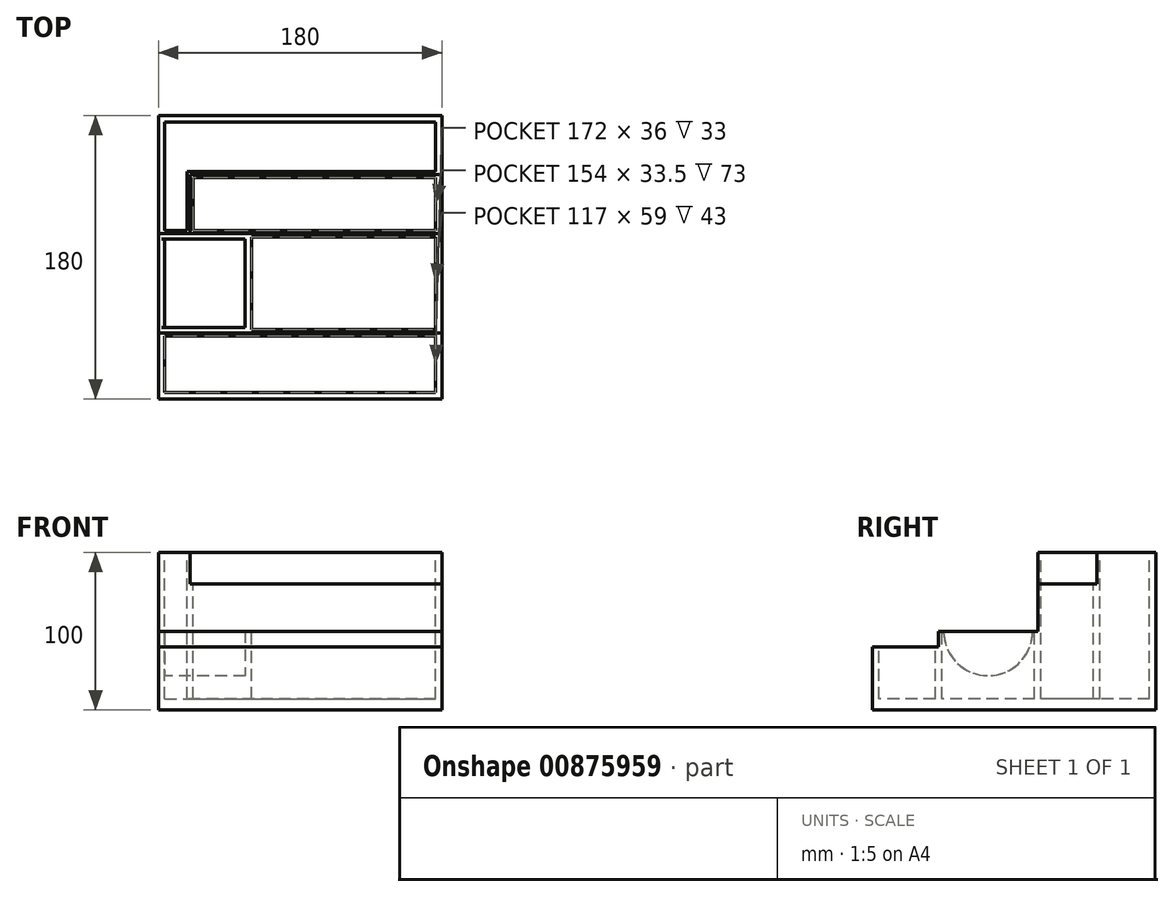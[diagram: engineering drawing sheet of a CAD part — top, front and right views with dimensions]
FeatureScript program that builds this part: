
annotation { "Feature Type Name" : "Feature", "Feature Type Description" : "" }
export const myFeature = defineFeature(function(context is Context, id is Id, definition is map)
    precondition{}
    {
        {
            var Q0;
            Q0=qCreatedBy(makeId("Top.planeOp"),FACE);
            var sketch = newSketch(context, id + "F0", { "sketchPlane" : qUnion([Q0])});
            skLineSegment(sketch, "E0.bottom", {"start": v(90, 90) * mm, "end": v(-90, 90) * mm});
            skLineSegment(sketch, "E0.top", {"start": v(90, -90) * mm, "end": v(-90, -90) * mm});
            skLineSegment(sketch, "E0.left", {"start": v(90, 90) * mm, "end": v(90, -90) * mm});
            skLineSegment(sketch, "E0.right", {"start": v(-90, 90) * mm, "end": v(-90, -90) * mm});
            skPoint(sketch, "E0.middle", {"position": v(0, 0) * mm});
            skLineSegment(sketch, "E1", {"start": v(-90, -48) * mm, "end": v(90, -48) * mm});
            skLineSegment(sketch, "E2", {"start": v(-90, 15) * mm, "end": v(90, 15) * mm});
            skLineSegment(sketch, "E3", {"start": v(-70, 52.5) * mm, "end": v(90, 52.5) * mm});
            skLineSegment(sketch, "E4", {"start": v(0, 15) * mm, "end": v(0, 90) * mm});
            skLineSegment(sketch, "E5", {"start": v(-70, 90) * mm, "end": v(-70, 15) * mm});
            skSolve(sketch);
        }
        {
            var Q0;
            {var subQ0=sQuery(id+"F0.wireOp",EDGE,"E4");var subQ1=sQuery(id+"F0.wireOp",EDGE,"E0.bottom");var subQ2=makeQuery(id+"F0.imprint","INTERSECT",VERTEX,{"derivedFrom":[subQ1,subQ0]});Q0=makeQuery(id+"F0.imprint","IMPRINT",FACE,{"disambiguationData":[TD([[makeQuery(id+"F0.imprint","IMPRINT",EDGE,{"disambiguationData":[TD([[subQ2,-1.0]])],"derivedFrom":subQ1}),1.0]])]});}
            var Q1;
            {var subQ0=sQuery(id+"F0.wireOp",EDGE,"E0.left");var subQ1=sQuery(id+"F0.wireOp",EDGE,"E0.bottom");var subQ2=makeQuery(id+"F0.imprint","INTERSECT",VERTEX,{"derivedFrom":[subQ1,subQ0]});Q1=makeQuery(id+"F0.imprint","IMPRINT",FACE,{"disambiguationData":[TD([[makeQuery(id+"F0.imprint","IMPRINT",EDGE,{"disambiguationData":[TD([[subQ2,-1.0]])],"derivedFrom":subQ1}),1.0]])]});}
            var Q2;
            {var subQ1=sQuery(id+"F0.wireOp",EDGE,"E0.right");var subQ5=sQuery(id+"F0.wireOp",EDGE,"E0.bottom");var subQ6=makeQuery(id+"F0.imprint","INTERSECT",VERTEX,{"derivedFrom":[subQ5,subQ1]});Q2=makeQuery(id+"F0.imprint","IMPRINT",FACE,{"disambiguationData":[TD([[makeQuery(id+"F0.imprint","IMPRINT",EDGE,{"disambiguationData":[TD([[subQ6,1.0]])],"derivedFrom":subQ5}),1.0]])]});}
            extrude(context, id + "F1", {"entities" : qUnion([Q0, Q1, Q2]), "depth" : 100 * mm, "offsetDistance" : 25 * mm});
        }
        {
            var Q0;
            {var subQ0=sQuery(id+"F0.wireOp",EDGE,"E4");var subQ1=sQuery(id+"F0.wireOp",EDGE,"E2");var subQ2=makeQuery(id+"F0.imprint","INTERSECT",VERTEX,{"derivedFrom":[subQ1,subQ0]});Q0=makeQuery(id+"F0.imprint","IMPRINT",FACE,{"disambiguationData":[TD([[makeQuery(id+"F0.imprint","IMPRINT",EDGE,{"disambiguationData":[TD([[subQ2,1.0]])],"derivedFrom":subQ1}),1.0]])]});}
            var Q1;
            {var subQ0=sQuery(id+"F0.wireOp",EDGE,"E2");var subQ1=sQuery(id+"F0.wireOp",EDGE,"E0.left");var subQ2=makeQuery(id+"F0.imprint","INTERSECT",VERTEX,{"derivedFrom":[subQ1,subQ0]});Q1=makeQuery(id+"F0.imprint","IMPRINT",FACE,{"disambiguationData":[TD([[makeQuery(id+"F0.imprint","IMPRINT",EDGE,{"disambiguationData":[TD([[subQ2,1.0]])],"derivedFrom":subQ1}),-1.0]])]});}
            extrude(context, id + "F2", {"entities" : qUnion([Q0, Q1]), "operationType" : NewBodyOperationType.ADD, "depth" : 80 * mm, "offsetDistance" : 25 * mm});
        }
        {
            var Q0;
            {var subQ0=sQuery(id+"F0.wireOp",EDGE,"E1");Q0=makeQuery(id+"F0.imprint","IMPRINT",FACE,{"disambiguationData":[TD([[makeQuery(id+"F0.imprint","IMPRINT",EDGE,{"derivedFrom":subQ0}),1.0]])]});}
            extrude(context, id + "F3", {"entities" : qUnion([Q0]), "operationType" : NewBodyOperationType.ADD, "depth" : 50 * mm, "offsetDistance" : 25 * mm});
        }
        {
            var Q0;
            {var subQ0=sQuery(id+"F0.wireOp",EDGE,"E0.top");Q0=makeQuery(id+"F0.imprint","IMPRINT",FACE,{"disambiguationData":[TD([[makeQuery(id+"F0.imprint","IMPRINT",EDGE,{"derivedFrom":subQ0}),-1.0]])]});}
            extrude(context, id + "F4", {"entities" : qUnion([Q0]), "operationType" : NewBodyOperationType.ADD, "depth" : 40 * mm, "offsetDistance" : 25 * mm});
        }
        {
            var Q0;
            Q0=makeQuery(id+"F1.opExtrude","CAP_FACE",FACE,{"disambiguationData":[OSD([sQuery(id+"F0.wireOp",EDGE,"E0.bottom"),sQuery(id+"F0.wireOp",EDGE,"E0.left"),sQuery(id+"F0.wireOp",EDGE,"E0.right"),sQuery(id+"F0.wireOp",EDGE,"E2"),sQuery(id+"F0.wireOp",EDGE,"E3"),sQuery(id+"F0.wireOp",EDGE,"E5")])],"isStart":false});
            cPlane(context, id + "F5", {"entities" : qUnion([Q0]), "cplaneType" : CPlaneType.OFFSET, "offset" : 0 * mm, "width" : 150 * mm, "height" : 150 * mm});
        }
        {
            var Q0;
            {var subQ0=sQuery(id+"F0.wireOp",EDGE,"E0.right");Q0=makeQuery(id+"F4.boolean.opBoolean","MERGE",FACE,{"derivedFrom":[makeQuery(id+"F3.boolean.opBoolean","MERGE",FACE,{"derivedFrom":[makeQuery(id+"F1.opExtrude","SWEPT_FACE",FACE,{"disambiguationData":[OSD([subQ0])]}),makeQuery(id+"F3.opExtrude","SWEPT_FACE",FACE,{"disambiguationData":[OSD([subQ0])]})]}),makeQuery(id+"F4.opExtrude","SWEPT_FACE",FACE,{"disambiguationData":[OSD([subQ0])]})]});}
            var sketch = newSketch(context, id + "F6", { "sketchPlane" : qUnion([Q0])});
            skCircle(sketch, "E6", {"center": v(16.5, 50) * mm, "radius": 28.25 * mm});
            skSolve(sketch);
        }
        {
            var Q0;
            {var subQ0=sQuery(id+"F6.wireOp",EDGE,"E6");var subQ1=makeQuery(id+"F3.opExtrude","CAP_EDGE",EDGE,{"disambiguationData":[OSD([sQuery(id+"F0.wireOp",EDGE,"E0.right")])],"isStart":false});var subQ2=makeQuery(id+"F6.imprint","INTERSECT",VERTEX,{"disambiguationData":[OD(0.0)],"derivedFrom":[subQ1,subQ0]});Q0=makeQuery(id+"F6.imprint","IMPRINT",FACE,{"disambiguationData":[TD([[makeQuery(id+"F6.imprint","IMPRINT",EDGE,{"disambiguationData":[TD([[subQ2,1.0]])],"derivedFrom":subQ0}),1.0]])]});}
            extrude(context, id + "F7", {"entities" : qUnion([Q0]), "operationType" : NewBodyOperationType.REMOVE, "oppositeDirection" : true, "depth" : 55 * mm, "offsetDistance" : 25 * mm});
        }
        {
            var Q0;
            {var subQ0=sQuery(id+"F6.wireOp",EDGE,"E6");var subQ1=makeQuery(id+"F3.opExtrude","CAP_EDGE",EDGE,{"disambiguationData":[OSD([sQuery(id+"F0.wireOp",EDGE,"E0.right")])],"isStart":false});var subQ2=makeQuery(id+"F6.imprint","INTERSECT",VERTEX,{"disambiguationData":[OD(0.0)],"derivedFrom":[subQ1,subQ0]});Q0=makeQuery(id+"F6.imprint","IMPRINT",FACE,{"disambiguationData":[TD([[makeQuery(id+"F6.imprint","IMPRINT",EDGE,{"disambiguationData":[TD([[subQ2,1.0]])],"derivedFrom":subQ0}),1.0]])]});}
            extrude(context, id + "F8", {"entities" : qUnion([Q0]), "operationType" : NewBodyOperationType.ADD, "oppositeDirection" : true, "depth" : 4 * mm, "offsetDistance" : 25 * mm});
        }
        {
            var Q0;
            Q0=makeQuery(id+"F4.opExtrude","SWEPT_FACE",FACE,{"disambiguationData":[OSD([sQuery(id+"F0.wireOp",EDGE,"E0.top")])]});
            var sketch = newSketch(context, id + "F9", { "sketchPlane" : qUnion([Q0])});
            skLineSegment(sketch, "E7", {"start": v(-90, 0) * mm, "end": v(-109.8, 0) * mm});
            skLineSegment(sketch, "E8", {"start": v(-109.8, 0) * mm, "end": v(-109.8, 85) * mm});
            skLineSegment(sketch, "E9", {"start": v(-109.8, 85) * mm, "end": v(-90, 85) * mm});
            skLineSegment(sketch, "E10", {"start": v(-90, 85) * mm, "end": v(-90, 0) * mm});
            skLineSegment(sketch, "E11.0", {"start": v(-107.4, 82.6) * mm, "end": v(-92.4, 82.6) * mm});
            skLineSegment(sketch, "E11.1", {"start": v(-107.4, 2.4) * mm, "end": v(-107.4, 82.6) * mm});
            skLineSegment(sketch, "E11.2", {"start": v(-92.4, 2.4) * mm, "end": v(-107.4, 2.4) * mm});
            skLineSegment(sketch, "E11.3", {"start": v(-92.4, 82.6) * mm, "end": v(-92.4, 2.4) * mm});
            skSolve(sketch);
        }
        {
            var Q0;
            Q0=makeQuery(id+"Fsurg89kKVSYqDt_1.opExtrude","SWEPT_EDGE",EDGE,{"disambiguationData":[OSD([sQuery(id+"F9.wireOp",EDGE,"E8"),sQuery(id+"F9.wireOp",EDGE,"E9")])]});
            var Q1;
            {var subQ0=sQuery(id+"F9.wireOp",EDGE,"E9");var subQ1=sQuery(id+"F9.wireOp",EDGE,"E10");Q1=makeQuery(id+"Fsurg89kKVSYqDt_1.boolean.opBoolean","SPLIT",EDGE,{"disambiguationData":[topologyDisambiguationEdgeConnected([makeQuery(id+"Fsurg89kKVSYqDt_1.opExtrude","SWEPT_FACE",FACE,{"disambiguationData":[OSD([subQ1])]})])],"derivedFrom":makeQuery(id+"Fsurg89kKVSYqDt_1.opExtrude","SWEPT_EDGE",EDGE,{"disambiguationData":[OSD([subQ0,subQ1])]})});}
            var Q2;
            Q2=makeQuery(id+"Fsurg89kKVSYqDt_1.opExtrude","CAP_EDGE",EDGE,{"disambiguationData":[OSD([sQuery(id+"F9.wireOp",EDGE,"E9")])],"isStart":true});
            var Q3;
            Q3=makeQuery(id+"Fsurg89kKVSYqDt_1.opExtrude","CAP_EDGE",EDGE,{"disambiguationData":[OSD([sQuery(id+"F9.wireOp",EDGE,"E9")])],"isStart":false});
            var Q4;
            {var subQ0=sQuery(id+"F6.wireOp",EDGE,"E6");var subQ1=sQuery(id+"F0.wireOp",EDGE,"E0.right");Q4=makeQuery(id+"F7.boolean.opBoolean","COPY",EDGE,{"derivedFrom":makeQuery(id+"F7.opExtrude","SWEPT_EDGE",EDGE,{"disambiguationData":[OSD([subQ1,subQ0]),TDD([makeQuery(id+"F6.imprint","INTERSECT",VERTEX,{"disambiguationData":[OD(1.0)],"derivedFrom":[makeQuery(id+"F3.opExtrude","CAP_EDGE",EDGE,{"disambiguationData":[OSD([subQ1])],"isStart":false}),subQ0]})])]})});}
            var Q5;
            Q5=makeQuery(id+"F7.boolean.opBoolean","COPY",EDGE,{"derivedFrom":makeQuery(id+"F7.opExtrude","CAP_EDGE",EDGE,{"disambiguationData":[OSD([sQuery(id+"F0.wireOp",EDGE,"E0.right")])],"isStart":false})});
            var Q6;
            {var subQ0=sQuery(id+"F6.wireOp",EDGE,"E6");var subQ1=sQuery(id+"F0.wireOp",EDGE,"E0.right");Q6=makeQuery(id+"F7.boolean.opBoolean","COPY",EDGE,{"derivedFrom":makeQuery(id+"F7.opExtrude","SWEPT_EDGE",EDGE,{"disambiguationData":[OSD([subQ1,subQ0]),TDD([makeQuery(id+"F6.imprint","INTERSECT",VERTEX,{"disambiguationData":[OD(0.0)],"derivedFrom":[makeQuery(id+"F3.opExtrude","CAP_EDGE",EDGE,{"disambiguationData":[OSD([subQ1])],"isStart":false}),subQ0]})])]})});}
            var Q7;
            Q7=makeQuery(id+"F8.opExtrude","CAP_EDGE",EDGE,{"disambiguationData":[OSD([sQuery(id+"F0.wireOp",EDGE,"E0.right")])],"isStart":false});
            fillet(context, id + "F10", {"entities" : qUnion([Q0, Q1, Q2, Q3, Q4, Q5, Q6, Q7]), "radius" : 2 * mm, "tangentPropagation" : true, "allowEdgeOverflow" : false});
        }
        {
            var Q0;
            Q0=qCreatedBy(id+"F5.planeOp",FACE);
            var sketch = newSketch(context, id + "F11", { "sketchPlane" : qUnion([Q0])});
            skLineSegment(sketch, "E12.0", {"start": v(-86, -48) * mm, "end": v(-86, -90) * mm});
            skLineSegment(sketch, "E13.0", {"start": v(86, -48) * mm, "end": v(86, -90) * mm});
            skLineSegment(sketch, "E14.0", {"start": v(90, -86) * mm, "end": v(-90, -86) * mm});
            skLineSegment(sketch, "E15.0", {"start": v(-90, -50) * mm, "end": v(90, -50) * mm});
            skLineSegment(sketch, "E16.0", {"start": v(-90, -46) * mm, "end": v(90, -46) * mm});
            skLineSegment(sketch, "E17.0", {"start": v(-31, 13.68) * mm, "end": v(-31, -46.68) * mm});
            skLineSegment(sketch, "E18.0", {"start": v(-70, 13) * mm, "end": v(90, 13) * mm});
            skLineSegment(sketch, "E19.0", {"start": v(-70, 17) * mm, "end": v(90, 17) * mm});
            skLineSegment(sketch, "E20.0", {"start": v(-68, 50.5) * mm, "end": v(-68, 15) * mm});
            skLineSegment(sketch, "E21.0", {"start": v(-68, 50.5) * mm, "end": v(90, 50.5) * mm});
            skLineSegment(sketch, "E22.0", {"start": v(86, 52.5) * mm, "end": v(86, 15) * mm});
            skLineSegment(sketch, "E23.0", {"start": v(86, 90) * mm, "end": v(86, 52.5) * mm});
            skLineSegment(sketch, "E24.0", {"start": v(90, 86) * mm, "end": v(-90, 86) * mm});
            skLineSegment(sketch, "E25.0", {"start": v(-86, 90) * mm, "end": v(-86, 15) * mm});
            skLineSegment(sketch, "E26.0", {"start": v(-90, 17) * mm, "end": v(-70, 17) * mm});
            skLineSegment(sketch, "E27.0", {"start": v(-72, 52.5) * mm, "end": v(-72, 15) * mm});
            skLineSegment(sketch, "E28.0", {"start": v(-70, 54.5) * mm, "end": v(90, 54.5) * mm});
            skLineSegment(sketch, "E29", {"start": v(-70, 54.5) * mm, "end": v(-72, 54.5) * mm});
            skLineSegment(sketch, "E30", {"start": v(-72, 52.5) * mm, "end": v(-72, 54.5) * mm});
            skLineSegment(sketch, "E31.0", {"start": v(86, 15) * mm, "end": v(86, -48) * mm});
            skSolve(sketch);
        }
        {
            var Q0;
            {var subQ12=sQuery(id+"F11.wireOp",EDGE,"E29");Q0=makeQuery(id+"F11.imprint","IMPRINT",FACE,{"disambiguationData":[TD([[makeQuery(id+"F11.imprint","IMPRINT",EDGE,{"derivedFrom":subQ12}),-1.0]])]});}
            var Q1;
            {var subQ0=sQuery(id+"F11.wireOp",EDGE,"E22.0");var subQ1=sQuery(id+"F11.wireOp",EDGE,"E19.0");var subQ2=makeQuery(id+"F11.imprint","INTERSECT",VERTEX,{"derivedFrom":[subQ1,subQ0]});Q1=makeQuery(id+"F11.imprint","IMPRINT",FACE,{"disambiguationData":[TD([[makeQuery(id+"F11.imprint","IMPRINT",EDGE,{"disambiguationData":[TD([[subQ2,1.0]])],"derivedFrom":subQ1}),1.0]])]});}
            var Q2;
            {var subQ0=sQuery(id+"F11.wireOp",EDGE,"E17.0");var subQ1=sQuery(id+"F11.wireOp",EDGE,"E16.0");var subQ2=makeQuery(id+"F11.imprint","INTERSECT",VERTEX,{"derivedFrom":[subQ1,subQ0]});Q2=makeQuery(id+"F11.imprint","IMPRINT",FACE,{"disambiguationData":[TD([[makeQuery(id+"F11.imprint","IMPRINT",EDGE,{"disambiguationData":[TD([[subQ2,-1.0]])],"derivedFrom":subQ1}),1.0]])]});}
            var Q3;
            {var subQ0=sQuery(id+"F11.wireOp",EDGE,"E14.0");var subQ1=sQuery(id+"F11.wireOp",EDGE,"E12.0");var subQ2=makeQuery(id+"F11.imprint","INTERSECT",VERTEX,{"derivedFrom":[subQ1,subQ0]});Q3=makeQuery(id+"F11.imprint","IMPRINT",FACE,{"disambiguationData":[TD([[makeQuery(id+"F11.imprint","IMPRINT",EDGE,{"disambiguationData":[TD([[subQ2,1.0]])],"derivedFrom":subQ1}),1.0]])]});}
            extrude(context, id + "F12", {"entities" : qUnion([Q0, Q1, Q2, Q3]), "operationType" : NewBodyOperationType.REMOVE, "oppositeDirection" : true, "depth" : 93 * mm, "offsetDistance" : 25 * mm});
        }
    });
